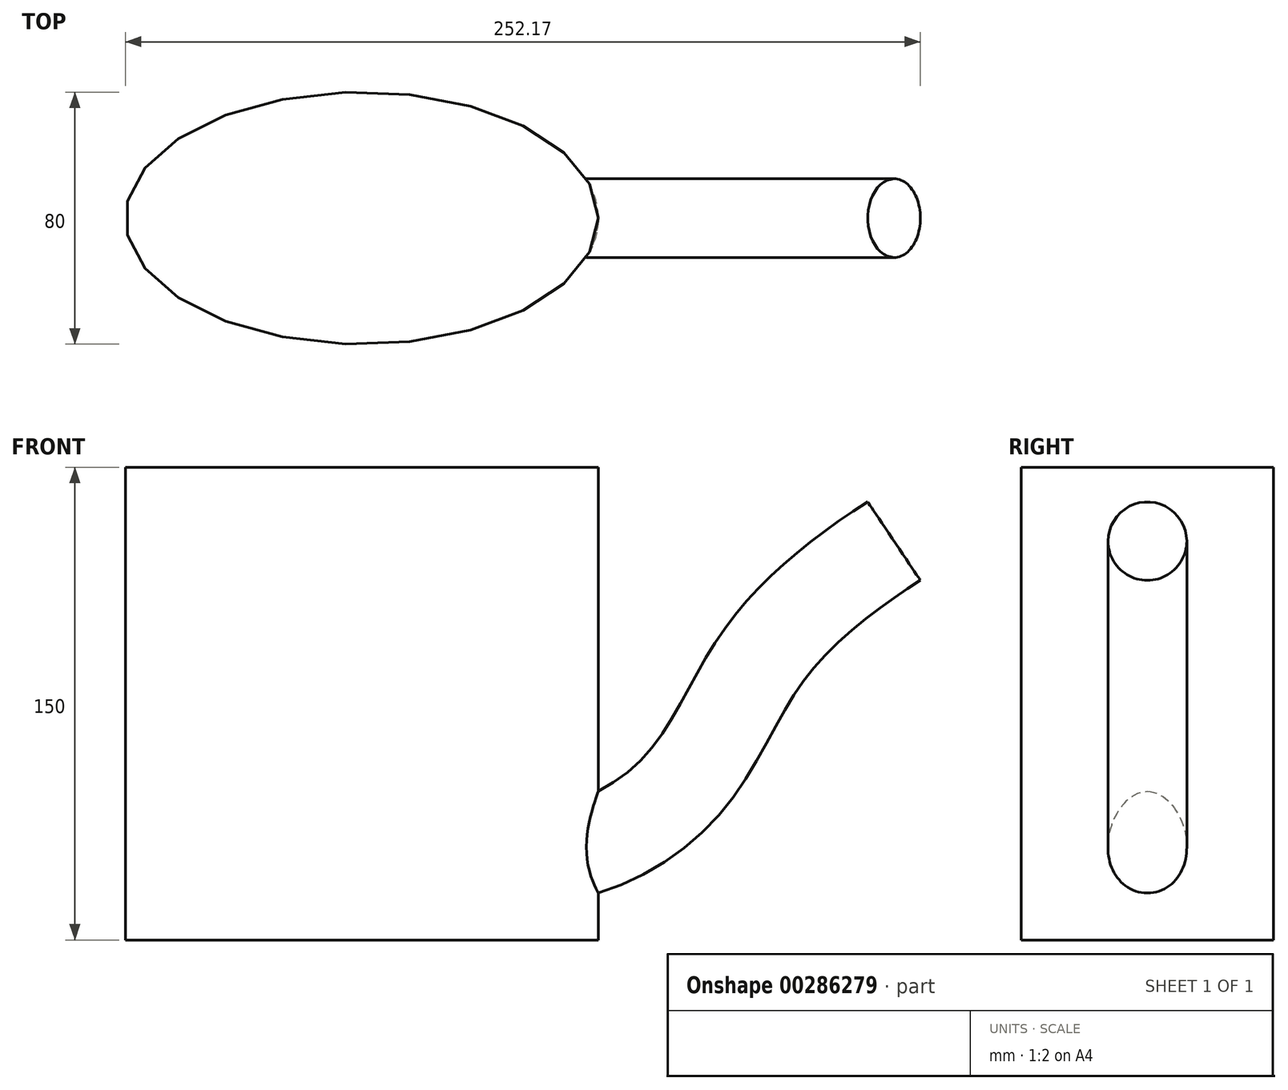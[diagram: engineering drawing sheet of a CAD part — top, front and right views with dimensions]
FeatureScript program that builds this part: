
annotation { "Feature Type Name" : "Feature", "Feature Type Description" : "" }
export const myFeature = defineFeature(function(context is Context, id is Id, definition is map)
    precondition{}
    {
        {
            var Q0;
            Q0=qCreatedBy(makeId("Top.planeOp"),FACE);
            var sketch = newSketch(context, id + "F0", { "sketchPlane" : qUnion([Q0])});
            skEllipse(sketch, "E0", {"center": v(0, 0) * mm, "majorRadius": 75 * mm, "minorRadius": 40 * mm, "majorAxis": v(1, 0)});
            skSolve(sketch);
        }
        {
            var Q0;
            Q0=makeQuery(id+"F0.imprint","IMPRINT",FACE,{"disambiguationData":[TD([[makeQuery(id+"F0.imprint","IMPRINT",EDGE,{"derivedFrom":sQuery(id+"F0.wireOp",EDGE,"E0")}),1.0]])]});
            extrude(context, id + "F1", {"entities" : qUnion([Q0]), "depth" : 150 * mm});
        }
        {
            var Q0;
            Q0=qCreatedBy(makeId("Front.planeOp"),FACE);
            var sketch = newSketch(context, id + "F2", { "sketchPlane" : qUnion([Q0])});
            skFitSpline(sketch, "E1", {"points": [v(53.01, 26.76) * mm, v(100.59, 47.97) * mm, v(129.14, 92.55) * mm, v(168.83, 126.54) * mm], "startDerivative": vector(155.78, -4.96) * mm, "endDerivative": vector(107, 66.95) * mm});
            skSolve(sketch);
        }
        {
            var Q0;
            Q0=qCreatedBy(makeId("Right.planeOp"),FACE);
            var sketch = newSketch(context, id + "F3", { "sketchPlane" : qUnion([Q0])});
            skPoint(sketch, "E2.0", {"position": v(0, 26.76) * mm});
            skEllipse(sketch, "E3", {"center": v(0, 26.76) * mm, "majorRadius": 15 * mm, "minorRadius": 12.5 * mm, "majorAxis": v(0, -1)});
            skSolve(sketch);
        }
        {
            var Q0;
            Q0=qCreatedBy(makeId("Right.planeOp"),FACE);
            cPlane(context, id + "F4", {"entities" : qUnion([Q0]), "cplaneType" : CPlaneType.OFFSET, "offset" : 53 * mm, "width" : 150 * mm, "height" : 150 * mm});
        }
        {
            var Q0;
            Q0=qCreatedBy(id+"F4.planeOp",FACE);
            var sketch = newSketch(context, id + "F5", { "sketchPlane" : qUnion([Q0])});
            skEllipse(sketch, "E4.0", {"center": v(0, 26.76) * mm, "majorRadius": 15 * mm, "minorRadius": 12.5 * mm, "majorAxis": v(0, -1)});
            skSolve(sketch);
        }
        {
            var Q0;
            Q0=qCreatedBy(makeId("Front.planeOp"),FACE);
            var sketch = newSketch(context, id + "F6", { "sketchPlane" : qUnion([Q0])});
            skLineSegment(sketch, "E5", {"start": v(158.5, 141.76) * mm, "end": v(184.6, 102.88) * mm});
            skSolve(sketch);
        }
        {
            var Q0;
            Q0=sQuery(id+"F6.wireOp",EDGE,"E5");
            cPlane(context, id + "F7", {"entities" : qUnion([Q0]), "cplaneType" : CPlaneType.LINE_ANGLE, "offset" : 25 * mm, "angle" : 0 * degree, "width" : 150 * mm, "height" : 150 * mm});
        }
        {
            var Q0;
            Q0 = qSketchRegion(id + "F5", true);
            var Q1;
            Q1=sQuery(id+"F2.wireOp",EDGE,"E1");
            sweep(context, id + "F8", {"operationType" : NewBodyOperationType.ADD, "profiles" : qUnion([Q0]), "path" : qUnion([Q1])});
        }
    });
